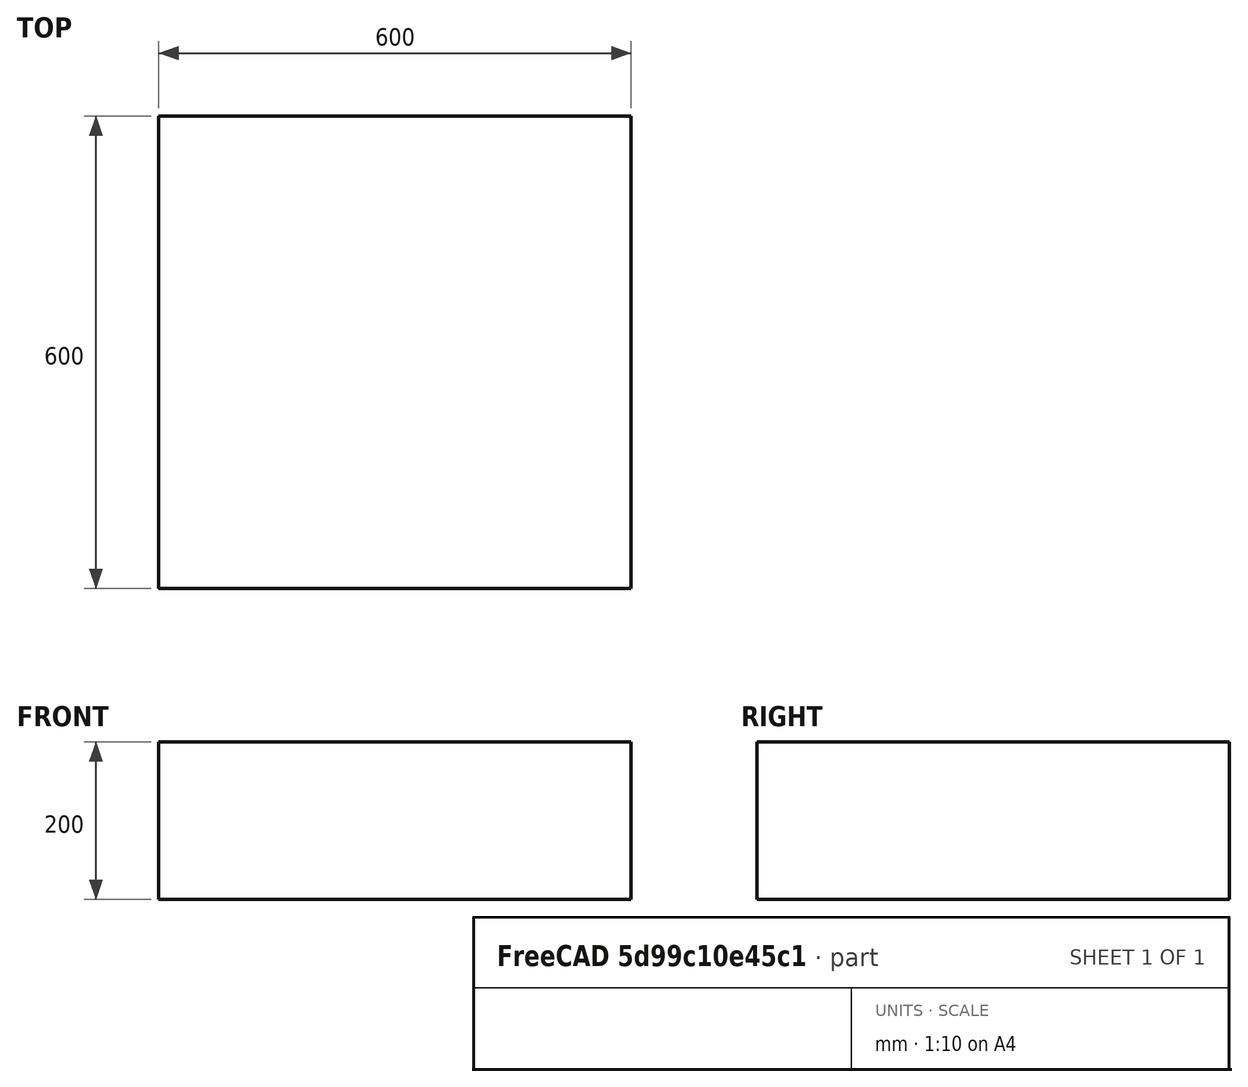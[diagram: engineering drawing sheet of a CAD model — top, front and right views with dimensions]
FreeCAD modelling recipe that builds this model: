
FCSTD DOCUMENT  (FreeCAD 0.19R24276 (Git))
Label: work-table
License: Creative Commons Attribution-ShareAlike
LicenseURL: http://creativecommons.org/licenses/by-sa/4.0/
objects: Sketcher::SketchObject×1, PartDesign::Pad×1, PartDesign::Body×1
note: 4 computed .brp shape members not serialized (recipe doc carries the construction recipe); baked Part::Feature solids carry a one-line shape summary decoded from their .brp

FEATURE [Sketcher::SketchObject] Sketch
  FullyConstrained = true
  MapMode = 5
  Support = -> [XY_Plane]
  sketch-geometry (5):
    g0: LineSegment StartX=-300 StartY=-300 StartZ=0 EndX=300 EndY=-300 EndZ=0
    g1: LineSegment StartX=300 StartY=-300 StartZ=0 EndX=300 EndY=300 EndZ=0
    g2: LineSegment StartX=300 StartY=300 StartZ=0 EndX=-300 EndY=300 EndZ=0
    g3: LineSegment StartX=-300 StartY=300 StartZ=0 EndX=-300 EndY=-300 EndZ=0
    g4: Circle CenterX=0 CenterY=0 CenterZ=0 NormalX=0 NormalY=0 NormalZ=1 AngleXU=0 Radius=424.264
  constraints (14):
    c: Coincident(g0,g1)
    c: Coincident(g1,g2)
    c: Coincident(g2,g3)
    c: Coincident(g3,g0)
    c: Equal(g0,g1)
    c: Equal(g0,g2)
    c: Equal(g0,g3)
    c: PointOnObject(g0,g4)
    c: PointOnObject(g1,g4)
    c: PointOnObject(g2,g4)
    c: PointOnObject(g3,g4)
    c: Coincident(g4,g-1)
    c: Horizontal(g0)
    c: Distance(g0) = 600
FEATURE [PartDesign::Pad] Pad
  Direction = (1,1,1)
  Length = 200
  Length2 = 100
  Profile = -> Sketch
  Type = 0
FEATURE [PartDesign::Body] Body
  Group = -> [Sketch,Pad]
  Origin = -> Origin
  Tip = -> Pad
